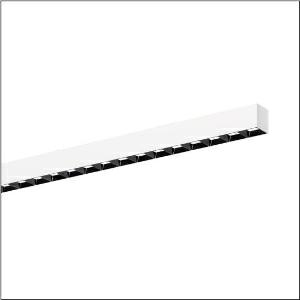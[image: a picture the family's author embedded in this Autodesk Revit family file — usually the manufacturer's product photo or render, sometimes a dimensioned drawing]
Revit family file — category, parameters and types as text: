
# Revit family: silica_r__21_51mx22tctaw_24f4
name_source: partatom
category: Lighting Fixtures
units: mm (PartAtom-declared; Revit-internal decimal feet)

## family parameters
Cut with Voids When Loaded = No
Host = Face
Light Source = No
Part Type = Normal
Room Calculation Point = No
Round Connector Dimension = Use Diameter
Shared = No

## types (1)
- --- (1 x LED, 9300 lm, 80.4 W, 6500K)
    Apparent Load = 80 VA
    CIE Flux Codes = 84 100 100 100 100
    Color Rendering = 80
    Color Temperature = 6500K
    Default Elevation = 1800 mm
    Description = Silica® 21, office luminaire, primary light control with darklight reflector, of PMMA, black, CAT 2 (L<= 3000cd/m²), light emission: direct distribution, primary light characteristic: symmetric, installation type: surface-mounted, LED, rated luminous flux: 9.300lm, luminous efficacy: 110lm/W, light colour: 8tw, colour temperature: 2700..6500K, control gear: ECG DALI, with terminal, 3+2-pole, max. 2.5mm², mains connection: 220..240V, AC, 50/60Hz, rated input power: 84.5W, luminaire housing, of aluminium, traffic white (RAL 9016), length: 3.004mm, width: 53mm, height: 53mm, protection rating (complete): IP20, insulation class (complete): insulation class I (protective earthing), certification: CE, permissible operating ambient temperature: 0..+35°C, standard: EN 50419, packaging unit: 1 piece
    Height = 0 mm  [stored 0 ft]
    Lamp = 1 x LED
    Lamp Light Flux = 9300 lm
    Lamp Power = 80.4 W
    Lamp count = 1
    Length = 3004 mm
    Luminous efficacy = 116 lm/W
    Manufacturer = Siteco
    ModVariant = No
    Model = 51MX22TCTAW
    Mounting Place = Ceiling
    Mounting Type = Recessed
    Number of Poles = 1
    OnlyDefault = Yes
    Power Factor = 1
    Product Name = Silica® 21
    Product group = office luminaire | ceiling recessed
    ProductGroupID = 401
    Protection Class = Protection class I
    Protection Degree = IP 20
    RLX_Detail_Level = 1
    RLX_Emergency_Light_Flux = 0 lm
    RLX_Emergency_Type = 0
    RLX_Emergency_Type_DB = No
    RlxData = <blob elided: 58237 chars, md5=1cfab3d9>
    Socket = socket
    Standby Power = 0 W
    System Light Flux = 9300 lm
    System Power = 80 W
    Type Comments = individual setting
    Type Image = l_1313592.jpg
    URL = http://relux.com
    VarID = @adj_089517
    Voltage = 0 V
    Weight = 0.00 kg
    Width = 53 mm

note: [stored X ft] marks values corroborated as IEEE doubles in the binary element streams (Revit-internal decimal feet)

## geometry (parser evidence)
native form markers: Blend x4, Sweep x10
no freeform markers — native parametric forms only
